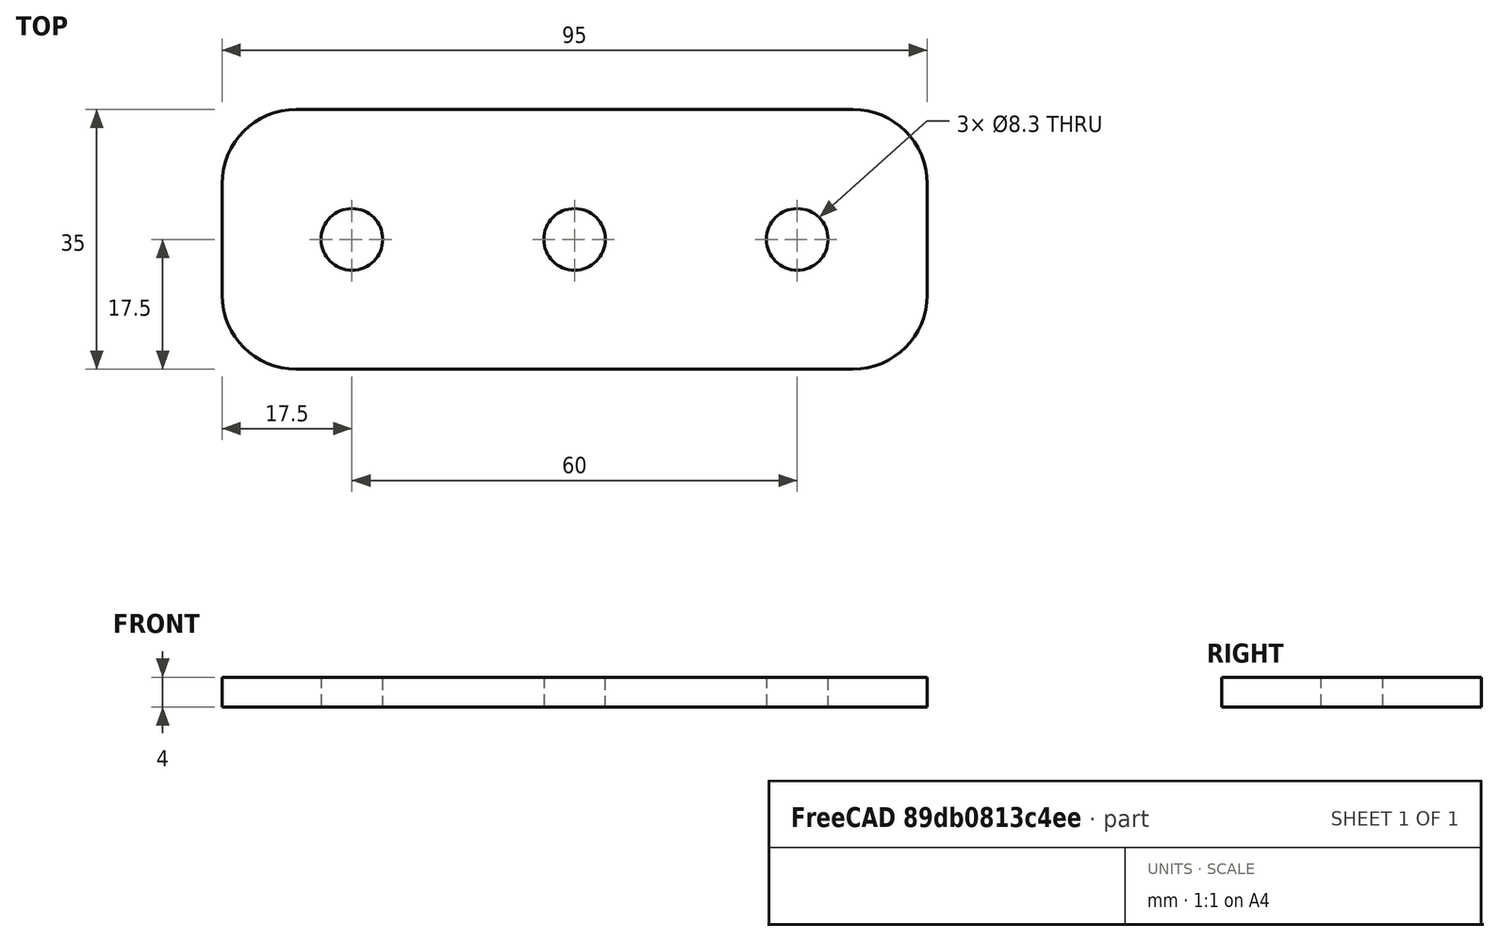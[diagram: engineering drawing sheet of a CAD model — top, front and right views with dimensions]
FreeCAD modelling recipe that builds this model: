
FCSTD DOCUMENT  (FreeCAD 0.19R24267 +99 (Git))
Label: V2 Allignment plate cap plate
License: All rights reserved
LicenseURL: http://en.wikipedia.org/wiki/All_rights_reserved
objects: Sketcher::SketchObject×1, PartDesign::Pad×1, PartDesign::Body×1
note: 4 computed .brp shape members not serialized (recipe doc carries the construction recipe); baked Part::Feature solids carry a one-line shape summary decoded from their .brp

FEATURE [Sketcher::SketchObject] Sketch
  FullyConstrained = true
  MapMode = 5
  Support = -> [XY_Plane]
  sketch-geometry (16):
    g0: Circle CenterX=0 CenterY=0 CenterZ=0 NormalX=0 NormalY=0 NormalZ=1 AngleXU=0 Radius=4.15
    g1: Circle CenterX=-30 CenterY=0 CenterZ=0 NormalX=0 NormalY=0 NormalZ=1 AngleXU=0 Radius=4.15
    g2: Circle CenterX=30 CenterY=0 CenterZ=0 NormalX=0 NormalY=0 NormalZ=1 AngleXU=0 Radius=4.15
    g3: LineSegment StartX=-37.5 StartY=17.5 StartZ=0 EndX=37.5 EndY=17.5 EndZ=0
    g4: LineSegment StartX=47.5 StartY=7.5 StartZ=0 EndX=47.5 EndY=-7.5 EndZ=0
    g5: LineSegment StartX=37.5 StartY=-17.5 StartZ=0 EndX=-37.5 EndY=-17.5 EndZ=0
    g6: LineSegment StartX=-47.5 StartY=-7.5 StartZ=0 EndX=-47.5 EndY=7.5 EndZ=0
    g7: ArcOfCircle CenterX=-37.5 CenterY=7.5 CenterZ=0 NormalX=0 NormalY=0 NormalZ=1 AngleXU=0 Radius=10 StartAngle=1.5708 EndAngle=3.14159
    g8: ArcOfCircle CenterX=-37.5 CenterY=-7.5 CenterZ=0 NormalX=0 NormalY=0 NormalZ=1 AngleXU=0 Radius=10 StartAngle=3.14159 EndAngle=4.71239
    g9: ArcOfCircle CenterX=37.5 CenterY=7.5 CenterZ=0 NormalX=0 NormalY=0 NormalZ=1 AngleXU=0 Radius=10 StartAngle=0 EndAngle=1.5708
    g10: ArcOfCircle CenterX=37.5 CenterY=-7.5 CenterZ=0 NormalX=0 NormalY=0 NormalZ=1 AngleXU=0 Radius=10 StartAngle=4.71239 EndAngle=6.28319
    g11: GeomPoint X=-47.5 Y=0 Z=0
    g12: GeomPoint X=0 Y=-4.15 Z=0
    g13: GeomPoint X=0 Y=-17.5 Z=0
    g14: LineSegment StartX=30 StartY=0 StartZ=0 EndX=30 EndY=-17.5 EndZ=0
    g15: LineSegment StartX=30 StartY=0 StartZ=0 EndX=47.5 EndY=0 EndZ=0
  constraints (37):
    c: Coincident(g0,g-1)
    c: PointOnObject(g1,g-1)
    c: Symmetric(g1,g2,g-2)
    c: DistanceX(g1,g2) = 60
    c: Equal(g1,g0)
    c: Equal(g0,g2)
    c: Diameter(g1) = 8.3
    c: Horizontal(g5)
    c: Vertical(g4)
    c: Tangent(g6,g7) = 1.5708
    c: Tangent(g3,g7) = 1.5708
    c: Tangent(g6,g8) = 1.5708
    c: Tangent(g5,g8) = 1.5708
    c: Tangent(g3,g9) = 1.5708
    c: Tangent(g4,g9) = 1.5708
    c: Tangent(g4,g10) = 1.5708
    c: Tangent(g5,g10) = 1.5708
    c: Equal(g8,g7)
    c: Equal(g7,g9)
    c: Equal(g9,g10)
    c: Symmetric(g6,g6,g-1)
    c: Symmetric(g3,g3,g-2)
    c: PointOnObject(g11,g6)
    c: PointOnObject(g11,g-1)
    c: PointOnObject(g13,g5)
    c: PointOnObject(g12,g0)
    c: PointOnObject(g12,g-2)
    c: PointOnObject(g13,g-2)
    c: Radius(g7) = 10
    c: DistanceY(g13,g0) = 17.5
    c: Coincident(g14,g2)
    c: PointOnObject(g14,g5)
    c: Coincident(g15,g2)
    c: PointOnObject(g15,g4)
    c: Horizontal(g15)
    c: Vertical(g14)
    c: Equal(g14,g15)
FEATURE [PartDesign::Pad] Pad  label="Thickness"
  Direction = (1,1,1)
  Length = 4
  Length2 = 100
  Profile = -> Sketch
  Type = 0
FEATURE [PartDesign::Body] Body
  Group = -> [Sketch,Pad]
  Origin = -> Origin
  Tip = -> Pad
